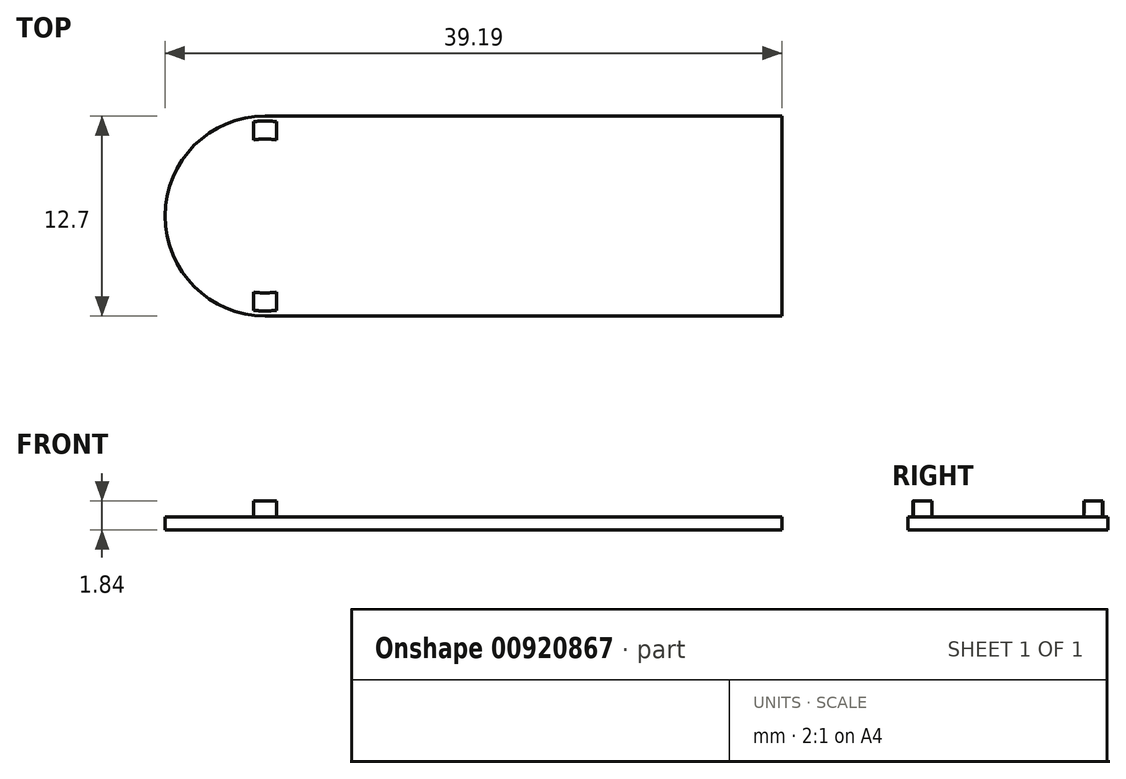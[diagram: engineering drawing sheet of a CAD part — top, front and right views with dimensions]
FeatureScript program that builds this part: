
annotation { "Feature Type Name" : "Feature", "Feature Type Description" : "" }
export const myFeature = defineFeature(function(context is Context, id is Id, definition is map)
    precondition{}
    {
        {
            var Q0;
            Q0=qCreatedBy(makeId("Top.planeOp"),FACE);
            var sketch = newSketch(context, id + "F0", { "sketchPlane" : qUnion([Q0])});
            skArc(sketch, "E0", {"start": v(0, 6.35) * mm, "mid": v(-6.35, 0) * mm, "end": v(0, -6.35) * mm});
            skLineSegment(sketch, "E1", {"start": v(0, 6.35) * mm, "end": v(32.84, 6.35) * mm});
            skLineSegment(sketch, "E2", {"start": v(32.84, 6.35) * mm, "end": v(32.84, -6.35) * mm});
            skLineSegment(sketch, "E3", {"start": v(32.84, -6.35) * mm, "end": v(0, -6.35) * mm});
            skSolve(sketch);
        }
        {
            var Q0;
            Q0 = qSketchRegion(id + "F0", true);
            extrude(context, id + "F1", {"entities" : qUnion([Q0]), "depth" : 0.83 * mm, "offsetDistance" : 25.4 * mm});
        }
        {
            var Q0;
            Q0=makeQuery(id+"F1.opExtrude","CAP_FACE",FACE,{"disambiguationData":[OSD([sQuery(id+"F0.wireOp",EDGE,"E0"),sQuery(id+"F0.wireOp",EDGE,"E1"),sQuery(id+"F0.wireOp",EDGE,"E2"),sQuery(id+"F0.wireOp",EDGE,"E3")])],"isStart":false});
            var sketch = newSketch(context, id + "F2", { "sketchPlane" : qUnion([Q0])});
            skArc(sketch, "E4", {"start": v(-0.72, -4.84) * mm, "mid": v(0, -4.89) * mm, "end": v(0.72, -4.84) * mm});
            skArc(sketch, "E5", {"start": v(-0.72, -5.99) * mm, "mid": v(0, -6.03) * mm, "end": v(0.72, -5.99) * mm});
            skLineSegment(sketch, "E6", {"start": v(-0.72, 5.99) * mm, "end": v(-0.72, 4.84) * mm});
            skLineSegment(sketch, "E7", {"start": v(0.72, 5.99) * mm, "end": v(0.72, 4.84) * mm});
            skLineSegment(sketch, "E8", {"start": v(0, 6.03) * mm, "end": v(0, -6.03) * mm, "construction": true});
            skPoint(sketch, "E9.orphan", {"position": v(0, 12.94) * mm});
            skArc(sketch, "E10.trimOffspring", {"start": v(0.72, 4.84) * mm, "mid": v(0, 4.89) * mm, "end": v(-0.72, 4.84) * mm});
            skArc(sketch, "E11.trimOffspring", {"start": v(0.72, 5.99) * mm, "mid": v(0, 6.03) * mm, "end": v(-0.72, 5.99) * mm});
            skLineSegment(sketch, "E12.trimOffspring", {"start": v(-0.72, -4.84) * mm, "end": v(-0.72, -5.99) * mm});
            skLineSegment(sketch, "E13.trimOffspring", {"start": v(0.72, -4.84) * mm, "end": v(0.72, -5.99) * mm});
            skSolve(sketch);
        }
        {
            var Q0;
            Q0 = qSketchRegion(id + "F2", true);
            extrude(context, id + "F3", {"entities" : qUnion([Q0]), "operationType" : NewBodyOperationType.ADD, "depth" : 1.02 * mm, "offsetDistance" : 25.4 * mm});
        }
    });
